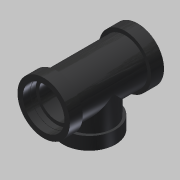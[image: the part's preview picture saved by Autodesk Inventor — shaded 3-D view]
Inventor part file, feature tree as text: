
AUTODESK INVENTOR PART (.ipt)
format: ipt  version: 2014 SP1 (Build 180222100, 222)  size: 190,976 bytes
history: native  units: in
note: dims shown in document units (in); Inventor stores cm internally (conversion verified against a paired STEP export)
features: sketch x8, extrude x7, fillet x1, plane x1, shell x1
ambient origin geometry x8: Origin, YZ Plane, XZ Plane, XY Plane, X Axis, Y Axis, Z Axis, Center Point
bodies: Body1 (feature_tree)
feature tree (18):
  extrude  "Extrusion2"  Depth=1.05in
  extrude  "Extrusion3"  Depth=2.2in
  fillet  "Fillet1"  Radius=1.05in
  plane  "Work Plane1"
  sketch  "Sketch8"  dims[d13=0.575in d14=0.475in d15=0.0in]
  extrude  "Extrusion4"  Depth=0.475in TaperAngle=0.0deg
  extrude  "Extrusion5"  [1 undecoded]
  extrude  "Extrusion6"  Depth=0.3in TaperAngle=0.0deg
  shell  "Shell1"  Thickness=1.225in
  extrude  "Extrusion7"  Depth=0.3in
  extrude  "Extrusion8"  Depth=0.12in
  sketch  "Sketch5"  dims[d7=1.05in d8=1.05in]
  sketch  "Sketch6"  dims[d9=2.2in d10=0.0in d11=1.05in d12=1.05in]
  sketch  "Sketch9"  dims[d16=0.525in d17=-0.3in]
  sketch  "Sketch10"  dims[d18=1.225in d19=0.3in d20=0.0in d21=1.225in]
  sketch  "Sketch11"  dims[d22=0.3in d23=0.0in d24=1.225in]
  sketch  "Sketch12"  dims[d25=0.3in d26=0.0in d27=0.12in]
  sketch  "Sketch13"  dims[d28=0.97in d29=0.3in d30=0.0in d31=0.97in d32=0.3in d33=0.0in d34=1.05in]
note: 1 required parameter value undecoded (feature->parameter linkage not recoverable at this tier; creation-order binding heuristic only, values carry confidence <= 0.55)
